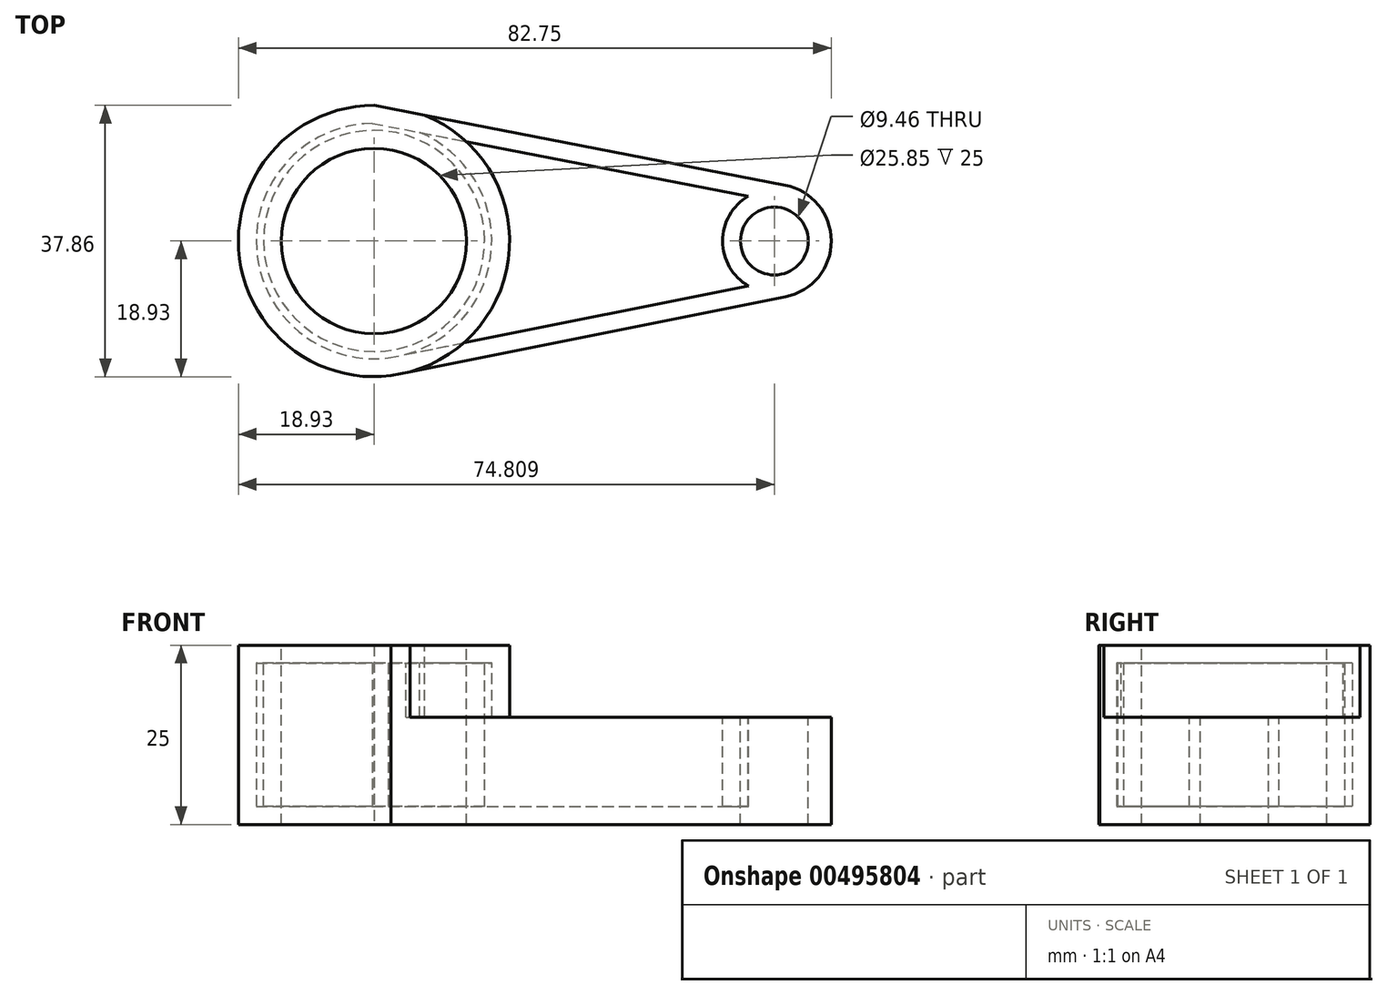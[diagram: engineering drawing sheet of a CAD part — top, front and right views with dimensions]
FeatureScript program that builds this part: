
annotation { "Feature Type Name" : "Feature", "Feature Type Description" : "" }
export const myFeature = defineFeature(function(context is Context, id is Id, definition is map)
    precondition{}
    {
        {
            var Q0;
            Q0=qCreatedBy(makeId("Top.planeOp"),FACE);
            var sketch = newSketch(context, id + "F0", { "sketchPlane" : qUnion([Q0])});
            skArc(sketch, "E0", {"start": v(7.08, 17.56) * mm, "mid": v(-18.9, 1.07) * mm, "end": v(5.05, -18.25) * mm});
            skArc(sketch, "E1", {"start": v(57.43, -7.79) * mm, "mid": v(63.82, 0.02) * mm, "end": v(57.4, 7.8) * mm});
            skLineSegment(sketch, "E2", {"start": v(0, 18.93) * mm, "end": v(57.4, 7.8) * mm});
            skLineSegment(sketch, "E3", {"start": v(2.35, -18.79) * mm, "end": v(57.43, -7.79) * mm});
            skPoint(sketch, "E4.end.orphan", {"position": v(29.9, -13.29) * mm});
            skSolve(sketch);
        }
        {
            var Q0;
            {var subQ3=sQuery(id+"F0.wireOp",EDGE,"E1");Q0=makeQuery(id+"F0.imprint","IMPRINT",FACE,{"disambiguationData":[TD([[makeQuery(id+"F0.imprint","IMPRINT",EDGE,{"derivedFrom":subQ3}),1.0]])]});}
            extrude(context, id + "F1", {"entities" : qUnion([Q0]), "depth" : 25 * mm});
        }
        {
            var Q0;
            Q0=makeQuery(id+"F1.opExtrude","CAP_FACE",FACE,{"disambiguationData":[OSD([sQuery(id+"F0.wireOp",EDGE,"E0"),sQuery(id+"F0.wireOp",EDGE,"E1"),sQuery(id+"F0.wireOp",EDGE,"E2"),sQuery(id+"F0.wireOp",EDGE,"E3")])],"isStart":false});
            var sketch = newSketch(context, id + "F2", { "sketchPlane" : qUnion([Q0])});
            skCircle(sketch, "E5", {"center": v(0, 0) * mm, "radius": 12.93 * mm});
            skCircle(sketch, "E6", {"center": v(55.88, 0) * mm, "radius": 4.73 * mm});
            skSolve(sketch);
        }
        {
            var Q0;
            Q0=makeQuery(id+"F2.imprint","IMPRINT",FACE,{"disambiguationData":[TD([[makeQuery(id+"F2.imprint","IMPRINT",EDGE,{"derivedFrom":sQuery(id+"F2.wireOp",EDGE,"E5")}),1.0]])]});
            var Q1;
            Q1=makeQuery(id+"F2.imprint","IMPRINT",FACE,{"disambiguationData":[TD([[makeQuery(id+"F2.imprint","IMPRINT",EDGE,{"derivedFrom":sQuery(id+"F2.wireOp",EDGE,"E6")}),1.0]])]});
            extrude(context, id + "F3", {"entities" : qUnion([Q0, Q1]), "operationType" : NewBodyOperationType.REMOVE, "oppositeDirection" : true, "depth" : 25 * mm});
        }
        {
            var Q0;
            Q0=makeQuery(id+"F1.opExtrude","CAP_FACE",FACE,{"disambiguationData":[OSD([sQuery(id+"F0.wireOp",EDGE,"E0"),sQuery(id+"F0.wireOp",EDGE,"E1"),sQuery(id+"F0.wireOp",EDGE,"E2"),sQuery(id+"F0.wireOp",EDGE,"E3")])],"isStart":false});
            var sketch = newSketch(context, id + "F4", { "sketchPlane" : qUnion([Q0])});
            skLineSegment(sketch, "E7.0", {"start": v(2.35, -18.79) * mm, "end": v(57.43, -7.79) * mm});
            skArc(sketch, "E8.0", {"start": v(0, 18.93) * mm, "mid": v(-18.9, -1.18) * mm, "end": v(2.35, -18.79) * mm});
            skLineSegment(sketch, "E9.0", {"start": v(0, 18.93) * mm, "end": v(57.4, 7.8) * mm});
            skArc(sketch, "E10.0", {"start": v(57.43, -7.79) * mm, "mid": v(63.82, 0.02) * mm, "end": v(57.4, 7.8) * mm});
            skCircle(sketch, "E11.0", {"center": v(55.88, 0) * mm, "radius": 4.73 * mm});
            skCircle(sketch, "E12.0", {"center": v(0, 0) * mm, "radius": 12.93 * mm});
            skCircle(sketch, "E13", {"center": v(0, 0) * mm, "radius": 18.93 * mm});
            skSolve(sketch);
        }
        {
            var Q0;
            {var subQ0=sQuery(id+"F4.wireOp",EDGE,"E10.0");Q0=makeQuery(id+"F4.imprint","IMPRINT",FACE,{"disambiguationData":[TD([[makeQuery(id+"F4.imprint","IMPRINT",EDGE,{"derivedFrom":subQ0}),1.0]])]});}
            extrude(context, id + "F5", {"entities" : qUnion([Q0]), "operationType" : NewBodyOperationType.REMOVE, "oppositeDirection" : true, "depth" : 10 * mm});
        }
        {
            var Q0;
            Q0=makeQuery(id+"F5.boolean.opBoolean","COPY",FACE,{"derivedFrom":makeQuery(id+"F5.opExtrude","CAP_FACE",FACE,{"disambiguationData":[OSD([sQuery(id+"F4.wireOp",EDGE,"E7.0"),sQuery(id+"F4.wireOp",EDGE,"E9.0"),sQuery(id+"F4.wireOp",EDGE,"E10.0"),sQuery(id+"F4.wireOp",EDGE,"E11.0"),sQuery(id+"F4.wireOp",EDGE,"E13")])],"isStart":false})});
            shell(context, id + "F6", {"entities" : qUnion([Q0]), "thickness" : 2.5 * mm});
        }
    });
